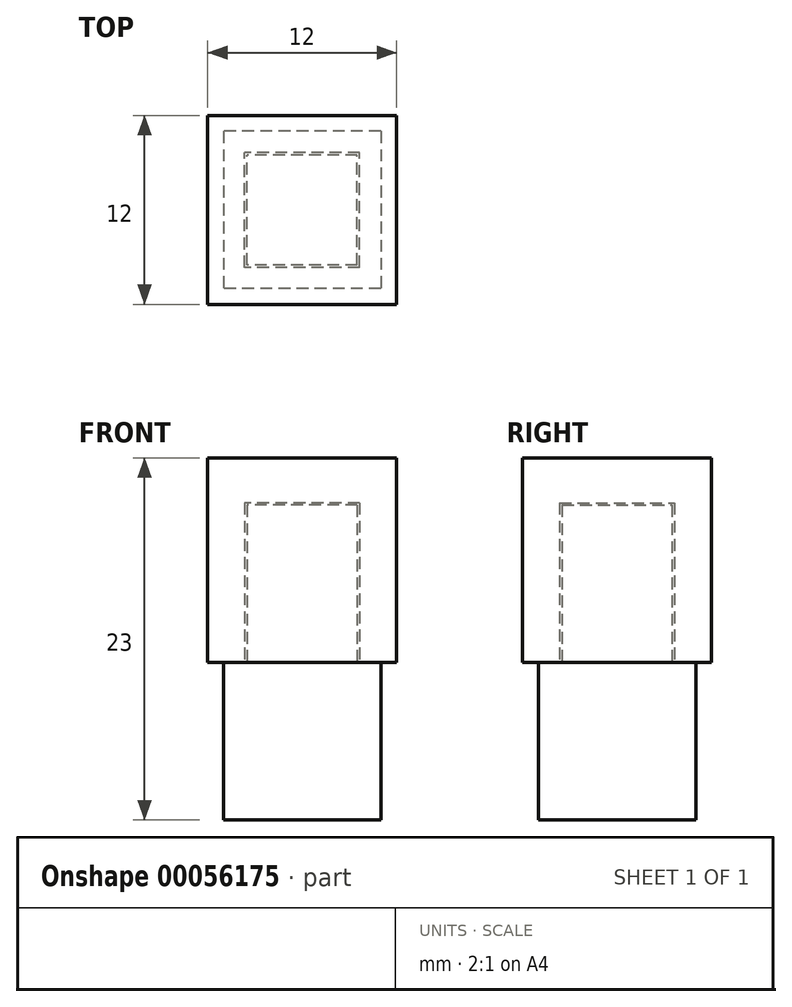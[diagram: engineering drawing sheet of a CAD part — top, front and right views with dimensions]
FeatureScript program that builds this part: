
annotation { "Feature Type Name" : "Feature", "Feature Type Description" : "" }
export const myFeature = defineFeature(function(context is Context, id is Id, definition is map)
    precondition{}
    {
        {
            var Q0;
            Q0=qCreatedBy(makeId("Top.planeOp"),FACE);
            var sketch = newSketch(context, id + "F0", { "sketchPlane" : qUnion([Q0])});
            skLineSegment(sketch, "E0.rect.bottom", {"start": v(5, 5) * mm, "end": v(-5, 5) * mm});
            skLineSegment(sketch, "E0.rect.top", {"start": v(5, -5) * mm, "end": v(-5, -5) * mm});
            skLineSegment(sketch, "E0.rect.left", {"start": v(5, 5) * mm, "end": v(5, -5) * mm});
            skLineSegment(sketch, "E0.rect.right", {"start": v(-5, 5) * mm, "end": v(-5, -5) * mm});
            skPoint(sketch, "E0.rect.middle", {"position": v(0, 0) * mm});
            skSolve(sketch);
        }
        {
            var Q0;
            Q0 = qSketchRegion(id + "F0", true);
            extrude(context, id + "F1", {"entities" : qUnion([Q0]), "depth" : 10 * mm});
        }
        {
            var Q0;
            Q0=makeQuery(id+"F1.opExtrude","CAP_FACE",FACE,{"disambiguationData":[OSD([sQuery(id+"F0.wireOp",EDGE,"E0.rect.bottom"),sQuery(id+"F0.wireOp",EDGE,"E0.rect.top"),sQuery(id+"F0.wireOp",EDGE,"E0.rect.left"),sQuery(id+"F0.wireOp",EDGE,"E0.rect.right")])],"isStart":false});
            var sketch = newSketch(context, id + "F2", { "sketchPlane" : qUnion([Q0])});
            skLineSegment(sketch, "E1.rect.bottom", {"start": v(3.5, -3.5) * mm, "end": v(-3.5, -3.5) * mm});
            skLineSegment(sketch, "E1.rect.top", {"start": v(3.5, 3.5) * mm, "end": v(-3.5, 3.5) * mm});
            skLineSegment(sketch, "E1.rect.left", {"start": v(3.5, -3.5) * mm, "end": v(3.5, 3.5) * mm});
            skLineSegment(sketch, "E1.rect.right", {"start": v(-3.5, -3.5) * mm, "end": v(-3.5, 3.5) * mm});
            skPoint(sketch, "E1.rect.middle", {"position": v(0, 0) * mm});
            skSolve(sketch);
        }
        {
            var Q0;
            Q0 = qSketchRegion(id + "F2", true);
            extrude(context, id + "F3", {"entities" : qUnion([Q0]), "operationType" : NewBodyOperationType.ADD, "depth" : 10 * mm});
        }
        {
            var Q0;
            Q0=makeQuery(id+"F1.opExtrude","CAP_FACE",FACE,{"disambiguationData":[OSD([sQuery(id+"F0.wireOp",EDGE,"E0.rect.bottom"),sQuery(id+"F0.wireOp",EDGE,"E0.rect.top"),sQuery(id+"F0.wireOp",EDGE,"E0.rect.left"),sQuery(id+"F0.wireOp",EDGE,"E0.rect.right")])],"isStart":false});
            var sketch = newSketch(context, id + "F4", { "sketchPlane" : qUnion([Q0])});
            skLineSegment(sketch, "E2.rect.bottom", {"start": v(6, -6) * mm, "end": v(-6, -6) * mm});
            skLineSegment(sketch, "E2.rect.top", {"start": v(6, 6) * mm, "end": v(-6, 6) * mm});
            skLineSegment(sketch, "E2.rect.left", {"start": v(6, -6) * mm, "end": v(6, 6) * mm});
            skLineSegment(sketch, "E2.rect.right", {"start": v(-6, -6) * mm, "end": v(-6, 6) * mm});
            skPoint(sketch, "E2.rect.middle", {"position": v(0, 0) * mm});
            skSolve(sketch);
        }
        {
            var Q0;
            Q0 = qSketchRegion(id + "F4", true);
            extrude(context, id + "F5", {"entities" : qUnion([Q0]), "depth" : 13 * mm});
        }
        {
            var Q0;
            Q0=makeQuery(id+"F1.opExtrude","SWEPT_BODY",BODY,{"disambiguationData":[OSD([sQuery(id+"F0.wireOp",EDGE,"E0.rect.bottom"),sQuery(id+"F0.wireOp",EDGE,"E0.rect.top"),sQuery(id+"F0.wireOp",EDGE,"E0.rect.left"),sQuery(id+"F0.wireOp",EDGE,"E0.rect.right")])]});
            var Q1;
            Q1=makeQuery(id+"F5.opExtrude","SWEPT_BODY",BODY,{"disambiguationData":[OSD([sQuery(id+"F4.wireOp",EDGE,"E2.rect.bottom"),sQuery(id+"F4.wireOp",EDGE,"E2.rect.top"),sQuery(id+"F4.wireOp",EDGE,"E2.rect.left"),sQuery(id+"F4.wireOp",EDGE,"E2.rect.right")])]});
            var Q2;
            Q2=makeQuery(id+"F3.opExtrude","SWEPT_FACE",FACE,{"disambiguationData":[OSD([sQuery(id+"F2.wireOp",EDGE,"E1.rect.bottom")])]});
            var Q3;
            Q3=makeQuery(id+"F3.opExtrude","SWEPT_FACE",FACE,{"disambiguationData":[OSD([sQuery(id+"F2.wireOp",EDGE,"E1.rect.right")])]});
            var Q4;
            Q4=makeQuery(id+"F3.opExtrude","CAP_FACE",FACE,{"disambiguationData":[OSD([sQuery(id+"F2.wireOp",EDGE,"E1.rect.bottom"),sQuery(id+"F2.wireOp",EDGE,"E1.rect.top"),sQuery(id+"F2.wireOp",EDGE,"E1.rect.left"),sQuery(id+"F2.wireOp",EDGE,"E1.rect.right")])],"isStart":false});
            var Q5;
            Q5=makeQuery(id+"F3.opExtrude","SWEPT_FACE",FACE,{"disambiguationData":[OSD([sQuery(id+"F2.wireOp",EDGE,"E1.rect.left")])]});
            var Q6;
            Q6=makeQuery(id+"F3.opExtrude","SWEPT_FACE",FACE,{"disambiguationData":[OSD([sQuery(id+"F2.wireOp",EDGE,"E1.rect.top")])]});
            booleanBodies(context, id + "F6", {"operationType" : BooleanOperationType.SUBTRACTION, "tools" : qUnion([Q0]), "targets" : qUnion([Q1]), "offset" : true, "entitiesToOffset" : qUnion([Q2, Q3, Q4, Q5, Q6]), "offsetDistance" : 0.15 * mm, "keepTools" : true});
        }
    });
